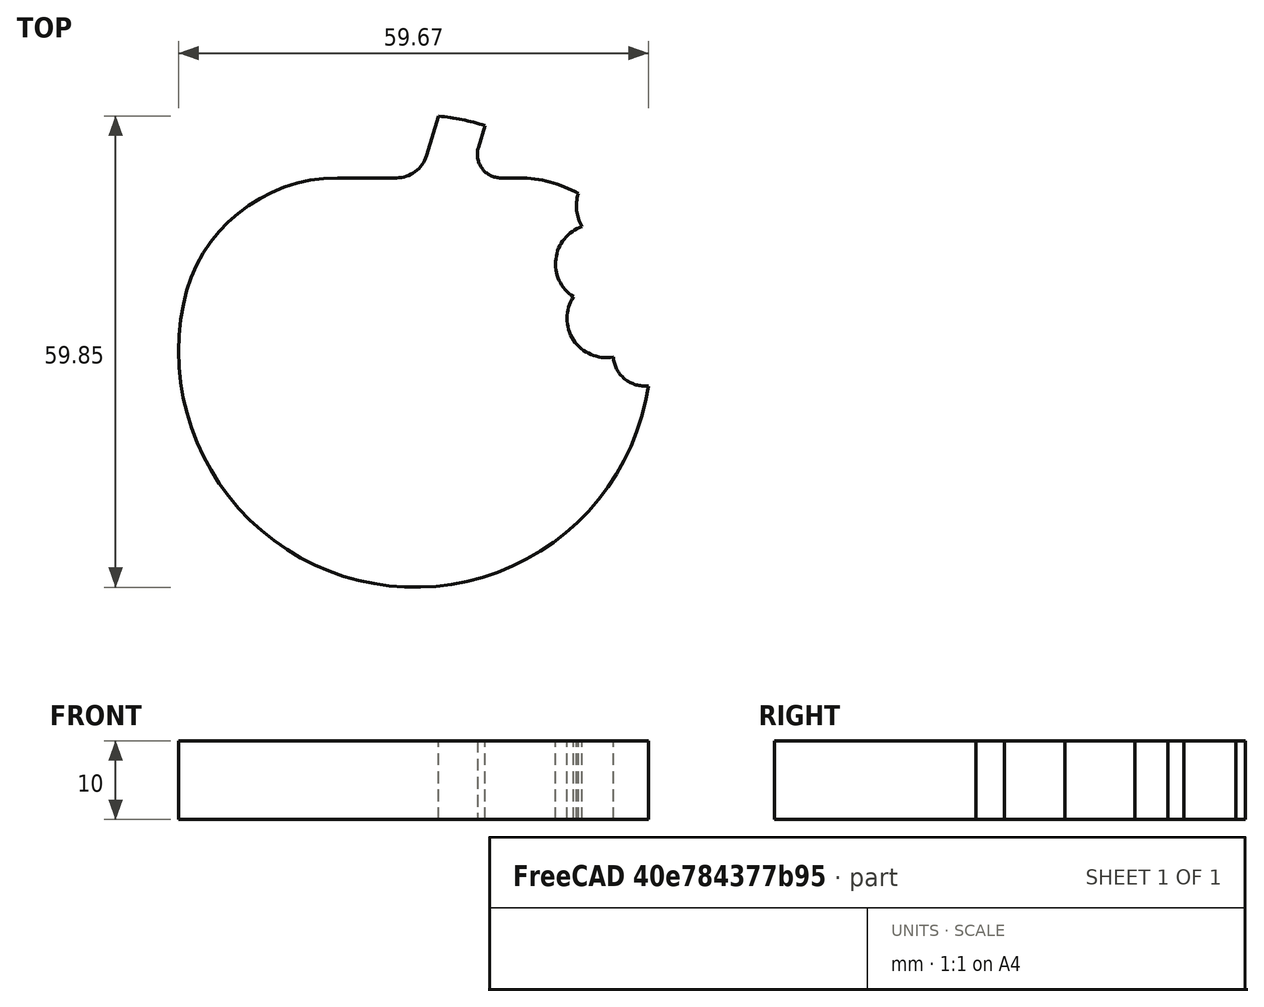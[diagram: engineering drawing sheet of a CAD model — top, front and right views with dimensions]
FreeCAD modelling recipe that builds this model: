
FCSTD DOCUMENT  (FreeCAD 0.15R4671 (Git))
Label: apple-cutter
License: All rights reserved
LicenseURL: http://en.wikipedia.org/wiki/All_rights_reserved
objects: Part::Cylinder×5, Part::Fillet×4, Part::Fuse×4, Part::Box×3, Part::Cut×3
note: 19 computed .brp shape members not serialized (recipe doc carries the construction recipe); baked Part::Feature solids carry a one-line shape summary decoded from their .brp

FEATURE [Part::Cylinder] Cylinder
  Angle = 360
  Height = 10
  Radius = 30
FEATURE [Part::Box] Box  label="Cube"
  Height = 15
  Length = 59
  Placement = pos=(-29,22,-3) rot=(0,0,1;0rad)
  Width = 14
FEATURE [Part::Box] Box001  label="Cube001"
  Height = 38
  Length = 6
  Placement = pos=(0,20,-14) rot=(0,0,-1;0.296706rad)
  Width = 25
FEATURE [Part::Cut] Cut
  Base = -> Box
  Tool = -> Box001
FEATURE [Part::Cut] Cut001
  Base = -> Cylinder
  Tool = -> Cut
FEATURE [Part::Fillet] Fillet
  Base = -> Cut001
  Edges = 1 edges r=20: [Edge3]
FEATURE [Part::Fillet] Fillet001
  Base = -> Fillet
  Edges = 1 edges r=15: [Edge15]
FEATURE [Part::Fillet] Fillet002
  Base = -> Fillet001
  Edges = 1 edges r=4: [Edge24]
FEATURE [Part::Fillet] Fillet003
  Base = -> Fillet002
  Edges = 1 edges r=3: [Edge27]
FEATURE [Part::Cylinder] Cylinder001
  Angle = 360
  Height = 15
  Placement = pos=(29,8,-3) rot=(0,0,1;0rad)
  Radius = 5
FEATURE [Part::Cylinder] Cylinder002
  Angle = 360
  Height = 15
  Placement = pos=(24,2,-3) rot=(0,0,1;0rad)
  Radius = 5
FEATURE [Part::Cylinder] Cylinder003
  Angle = 360
  Height = 15
  Placement = pos=(23,-5,-3) rot=(0,0,1;0rad)
  Radius = 5
FEATURE [Part::Cylinder] Cylinder004
  Angle = 360
  Height = 15
  Placement = pos=(26,-11,-3) rot=(0,0,1;0rad)
  Radius = 4
FEATURE [Part::Box] Box002  label="Cube002"
  Height = 15
  Length = 10
  Placement = pos=(23,-9,-2) rot=(0,0,1;0rad)
  Width = 14
FEATURE [Part::Fuse] Fusion
  Base = -> Cylinder002
  Tool = -> Box002
FEATURE [Part::Fuse] Fusion001
  Base = -> Cylinder001
  Tool = -> Fusion
FEATURE [Part::Fuse] Fusion002
  Base = -> Cylinder004
  Tool = -> Fusion001
FEATURE [Part::Fuse] Fusion003
  Base = -> Cylinder003
  Placement = pos=(1,1,0) rot=(0,0,1;0.349066rad)
  Tool = -> Fusion002
FEATURE [Part::Cut] Cut002
  Base = -> Fillet003
  Tool = -> Fusion003
